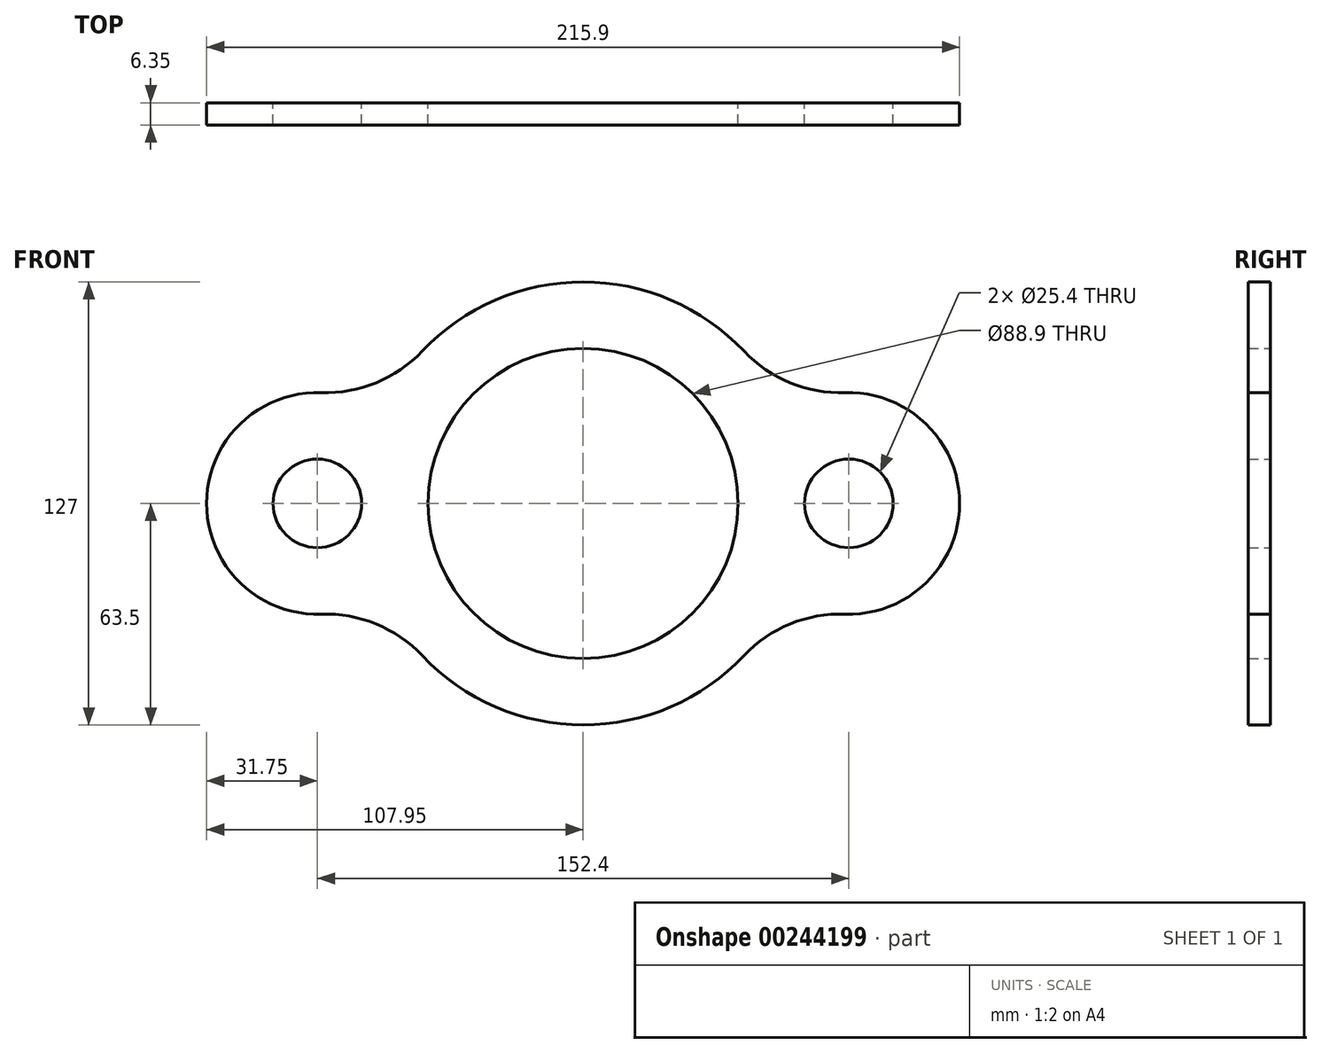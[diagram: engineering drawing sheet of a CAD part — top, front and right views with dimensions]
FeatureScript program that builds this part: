
annotation { "Feature Type Name" : "Feature", "Feature Type Description" : "" }
export const myFeature = defineFeature(function(context is Context, id is Id, definition is map)
    precondition{}
    {
        {
            var Q0;
            Q0=qCreatedBy(makeId("Front.planeOp"),FACE);
            var sketch = newSketch(context, id + "F0", { "sketchPlane" : qUnion([Q0])});
            skCircle(sketch, "E0", {"center": v(0, 0) * mm, "radius": 44.45 * mm});
            skArc(sketch, "E1", {"start": v(-46.14, -43.63) * mm, "mid": v(0, -63.5) * mm, "end": v(46.14, -43.63) * mm});
            skCircle(sketch, "E2", {"center": v(76.2, 0) * mm, "radius": 12.7 * mm});
            skArc(sketch, "E3", {"start": v(75.12, -31.73) * mm, "mid": v(107.95, 0) * mm, "end": v(75.12, 31.73) * mm});
            skCircle(sketch, "E4", {"center": v(-76.2, 0) * mm, "radius": 12.7 * mm});
            skArc(sketch, "E5", {"start": v(-75.12, 31.73) * mm, "mid": v(-107.95, 0) * mm, "end": v(-75.12, -31.73) * mm});
            skArc(sketch, "E6.trimOffspring", {"start": v(46.14, 43.63) * mm, "mid": v(0, 63.5) * mm, "end": v(-46.14, 43.63) * mm});
            skPoint(sketch, "E7.visualSharp", {"position": v(-57.94, 25.98) * mm});
            skArc(sketch, "E7.filletArc", {"start": v(-75.12, 31.73) * mm, "mid": v(-59.35, 34.56) * mm, "end": v(-46.14, 43.63) * mm});
            skPoint(sketch, "E8.visualSharp", {"position": v(57.94, 25.98) * mm});
            skArc(sketch, "E8.filletArc", {"start": v(46.14, 43.63) * mm, "mid": v(59.35, 34.56) * mm, "end": v(75.12, 31.73) * mm});
            skPoint(sketch, "E9.visualSharp", {"position": v(57.94, -25.98) * mm});
            skArc(sketch, "E9.filletArc", {"start": v(75.12, -31.73) * mm, "mid": v(59.35, -34.56) * mm, "end": v(46.14, -43.63) * mm});
            skPoint(sketch, "E10.visualSharp", {"position": v(-57.94, -25.98) * mm});
            skArc(sketch, "E10.filletArc", {"start": v(-46.14, -43.63) * mm, "mid": v(-59.35, -34.56) * mm, "end": v(-75.12, -31.73) * mm});
            skSolve(sketch);
        }
        {
            var Q0;
            Q0 = qSketchRegion(id + "F0", true);
            extrude(context, id + "F1", {"entities" : qUnion([Q0]), "depth" : 6.35 * mm});
        }
    });
